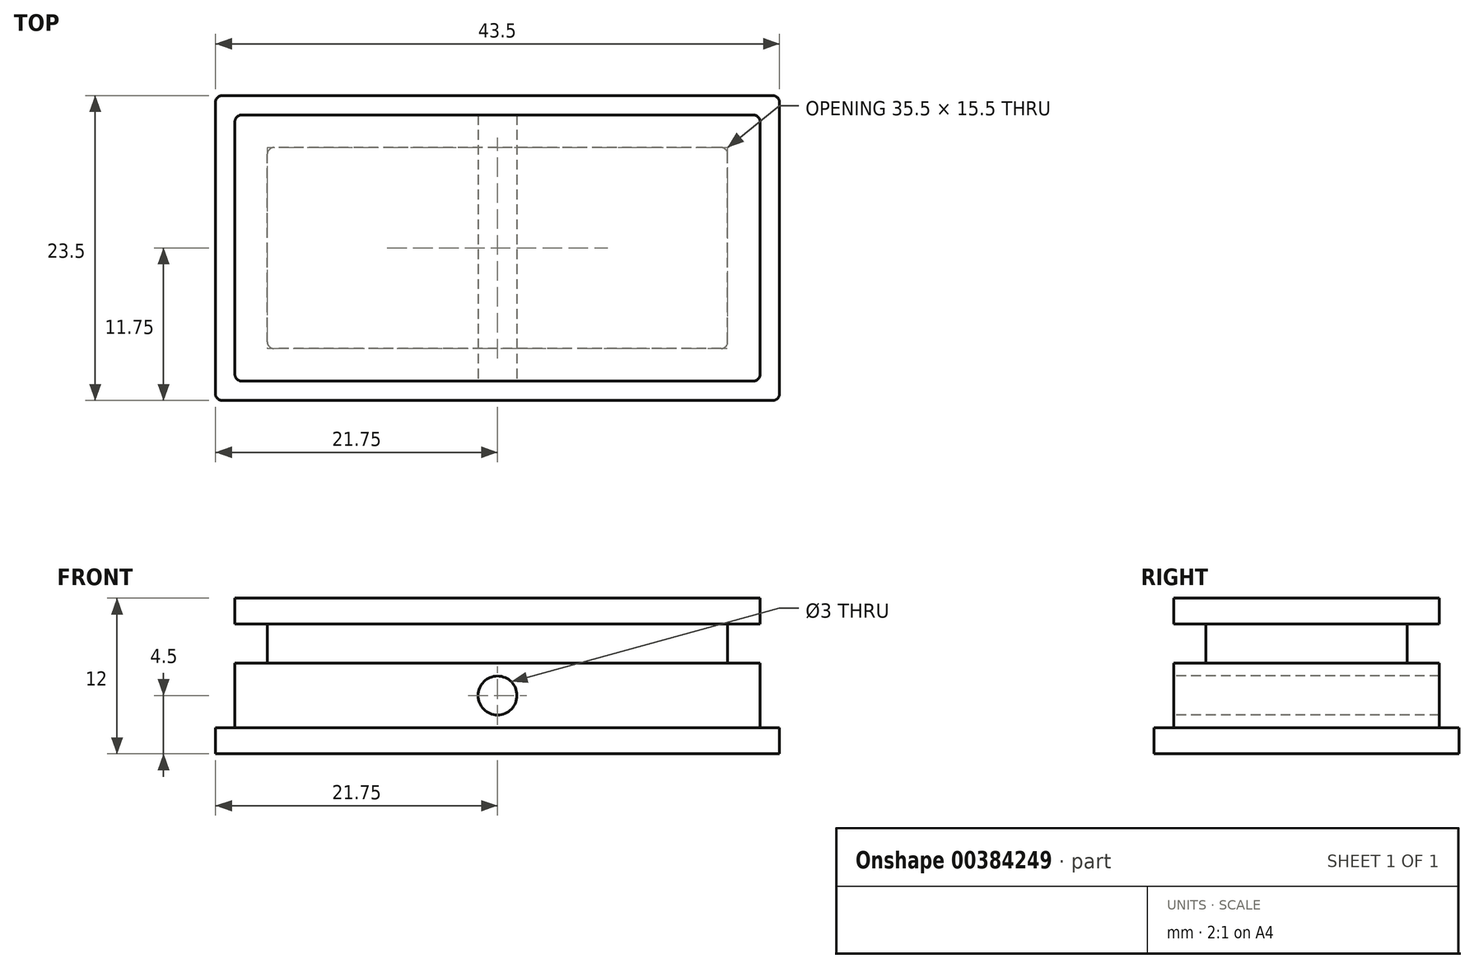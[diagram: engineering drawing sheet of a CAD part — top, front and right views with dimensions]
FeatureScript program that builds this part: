
annotation { "Feature Type Name" : "Feature", "Feature Type Description" : "" }
export const myFeature = defineFeature(function(context is Context, id is Id, definition is map)
    precondition{}
    {
        {
            var Q0;
            Q0=qCreatedBy(makeId("Top.planeOp"),FACE);
            var sketch = newSketch(context, id + "F0", { "sketchPlane" : qUnion([Q0])});
            skLineSegment(sketch, "E0.bottom", {"start": v(21.75, -11.75) * mm, "end": v(-21.75, -11.75) * mm});
            skLineSegment(sketch, "E0.top", {"start": v(21.75, 11.75) * mm, "end": v(-21.75, 11.75) * mm});
            skLineSegment(sketch, "E0.left", {"start": v(21.75, -11.75) * mm, "end": v(21.75, 11.75) * mm});
            skLineSegment(sketch, "E0.right", {"start": v(-21.75, -11.75) * mm, "end": v(-21.75, 11.75) * mm});
            skPoint(sketch, "E0.middle", {"position": v(0, 0) * mm});
            skSolve(sketch);
        }
        {
            var Q0;
            Q0=qSketchRegion(id+"F0",true);
            extrude(context, id + "F1", {"entities" : qUnion([Q0]), "depth" : 2 * mm});
        }
        {
            var Q0;
            Q0=makeQuery(id+"F1.opExtrude","CAP_FACE",FACE,{"disambiguationData":[OSD([sQuery(id+"F0.wireOp",EDGE,"E0.bottom"),sQuery(id+"F0.wireOp",EDGE,"E0.top"),sQuery(id+"F0.wireOp",EDGE,"E0.left"),sQuery(id+"F0.wireOp",EDGE,"E0.right")])],"isStart":false});
            var sketch = newSketch(context, id + "F2", { "sketchPlane" : qUnion([Q0])});
            skLineSegment(sketch, "E1.bottom", {"start": v(21.75, -11.75) * mm, "end": v(-21.75, -11.75) * mm, "construction": true});
            skLineSegment(sketch, "E1.top", {"start": v(21.75, 11.75) * mm, "end": v(-21.75, 11.75) * mm, "construction": true});
            skLineSegment(sketch, "E1.left", {"start": v(21.75, -11.75) * mm, "end": v(21.75, 11.75) * mm, "construction": true});
            skLineSegment(sketch, "E1.right", {"start": v(-21.75, -11.75) * mm, "end": v(-21.75, 11.75) * mm, "construction": true});
            skPoint(sketch, "E1.middle", {"position": v(0, 0) * mm});
            skLineSegment(sketch, "E2.0", {"start": v(20.25, 10.25) * mm, "end": v(-20.25, 10.25) * mm});
            skLineSegment(sketch, "E2.1", {"start": v(20.25, -10.25) * mm, "end": v(20.25, 10.25) * mm});
            skLineSegment(sketch, "E2.2", {"start": v(20.25, -10.25) * mm, "end": v(-20.25, -10.25) * mm});
            skLineSegment(sketch, "E2.3", {"start": v(-20.25, -10.25) * mm, "end": v(-20.25, 10.25) * mm});
            skSolve(sketch);
        }
        {
            var Q0;
            Q0=qSketchRegion(id+"F2",true);
            extrude(context, id + "F3", {"entities" : qUnion([Q0]), "operationType" : NewBodyOperationType.ADD, "depth" : 5 * mm});
        }
        {
            var Q0;
            Q0=makeQuery(id+"F3.opExtrude","CAP_FACE",FACE,{"disambiguationData":[OSD([sQuery(id+"F2.wireOp",EDGE,"E2.0"),sQuery(id+"F2.wireOp",EDGE,"E2.1"),sQuery(id+"F2.wireOp",EDGE,"E2.2"),sQuery(id+"F2.wireOp",EDGE,"E2.3")])],"isStart":false});
            var sketch = newSketch(context, id + "F4", { "sketchPlane" : qUnion([Q0])});
            skLineSegment(sketch, "E3.0", {"start": v(20.25, -10.25) * mm, "end": v(-20.25, -10.25) * mm, "construction": true});
            skLineSegment(sketch, "E4.0", {"start": v(-20.25, -10.25) * mm, "end": v(-20.25, 10.25) * mm, "construction": true});
            skLineSegment(sketch, "E5.0", {"start": v(20.25, 10.25) * mm, "end": v(-20.25, 10.25) * mm, "construction": true});
            skLineSegment(sketch, "E6.0", {"start": v(20.25, -10.25) * mm, "end": v(20.25, 10.25) * mm, "construction": true});
            skLineSegment(sketch, "E7.0", {"start": v(-17.75, -7.75) * mm, "end": v(-17.75, 7.75) * mm});
            skLineSegment(sketch, "E7.1", {"start": v(17.75, -7.75) * mm, "end": v(-17.75, -7.75) * mm});
            skLineSegment(sketch, "E7.2", {"start": v(17.75, -7.75) * mm, "end": v(17.75, 7.75) * mm});
            skLineSegment(sketch, "E7.3", {"start": v(17.75, 7.75) * mm, "end": v(-17.75, 7.75) * mm});
            skSolve(sketch);
        }
        {
            var Q0;
            Q0=qSketchRegion(id+"F4",true);
            var Q1;
            Q1=qConstructionFilter(qBodyType(qCreatedBy(id+"F4",EDGE),BodyType.WIRE),ConstructionObject.NO);
            extrude(context, id + "F5", {"entities" : qUnion([Q0]), "operationType" : NewBodyOperationType.ADD, "surfaceEntities" : qUnion([Q1]), "depth" : 3 * mm});
        }
        {
            var Q0;
            Q0=makeQuery(id+"F5.opExtrude","CAP_FACE",FACE,{"disambiguationData":[OSD([sQuery(id+"F4.wireOp",EDGE,"E7.0"),sQuery(id+"F4.wireOp",EDGE,"E7.1"),sQuery(id+"F4.wireOp",EDGE,"E7.2"),sQuery(id+"F4.wireOp",EDGE,"E7.3")])],"isStart":false});
            var sketch = newSketch(context, id + "F6", { "sketchPlane" : qUnion([Q0])});
            skLineSegment(sketch, "E8.0", {"start": v(20.25, -10.25) * mm, "end": v(-20.25, -10.25) * mm});
            skLineSegment(sketch, "E9.0", {"start": v(20.25, -10.25) * mm, "end": v(20.25, 10.25) * mm});
            skLineSegment(sketch, "E10.0", {"start": v(20.25, 10.25) * mm, "end": v(-20.25, 10.25) * mm});
            skLineSegment(sketch, "E10.1", {"start": v(-20.25, -10.25) * mm, "end": v(-20.25, 10.25) * mm});
            skSolve(sketch);
        }
        {
            var Q0;
            Q0=qSketchRegion(id+"F6",true);
            extrude(context, id + "F7", {"entities" : qUnion([Q0]), "operationType" : NewBodyOperationType.ADD, "depth" : 2 * mm});
        }
        {
            var Q0;
            Q0=makeQuery(id+"F3.opExtrude","SWEPT_EDGE",EDGE,{"disambiguationData":[OSD([sQuery(id+"F2.wireOp",EDGE,"E2.0"),sQuery(id+"F2.wireOp",EDGE,"E2.3")])]});
            var Q1;
            Q1=makeQuery(id+"F5.opExtrude","SWEPT_EDGE",EDGE,{"disambiguationData":[OSD([sQuery(id+"F4.wireOp",EDGE,"E7.0"),sQuery(id+"F4.wireOp",EDGE,"E7.3")])]});
            var Q2;
            Q2=makeQuery(id+"F7.opExtrude","SWEPT_EDGE",EDGE,{"disambiguationData":[OSD([sQuery(id+"F6.wireOp",EDGE,"E10.0"),sQuery(id+"F6.wireOp",EDGE,"E10.1")])]});
            var Q3;
            Q3=makeQuery(id+"F3.opExtrude","SWEPT_EDGE",EDGE,{"disambiguationData":[OSD([sQuery(id+"F2.wireOp",EDGE,"E2.2"),sQuery(id+"F2.wireOp",EDGE,"E2.3")])]});
            var Q4;
            Q4=makeQuery(id+"F5.opExtrude","SWEPT_EDGE",EDGE,{"disambiguationData":[OSD([sQuery(id+"F4.wireOp",EDGE,"E7.0"),sQuery(id+"F4.wireOp",EDGE,"E7.1")])]});
            var Q5;
            Q5=makeQuery(id+"F7.opExtrude","SWEPT_EDGE",EDGE,{"disambiguationData":[OSD([sQuery(id+"F6.wireOp",EDGE,"E8.0"),sQuery(id+"F6.wireOp",EDGE,"E10.1")])]});
            var Q6;
            Q6=makeQuery(id+"F3.opExtrude","SWEPT_EDGE",EDGE,{"disambiguationData":[OSD([sQuery(id+"F2.wireOp",EDGE,"E2.1"),sQuery(id+"F2.wireOp",EDGE,"E2.2")])]});
            var Q7;
            Q7=makeQuery(id+"F5.opExtrude","SWEPT_EDGE",EDGE,{"disambiguationData":[OSD([sQuery(id+"F4.wireOp",EDGE,"E7.1"),sQuery(id+"F4.wireOp",EDGE,"E7.2")])]});
            var Q8;
            Q8=makeQuery(id+"F7.opExtrude","SWEPT_EDGE",EDGE,{"disambiguationData":[OSD([sQuery(id+"F6.wireOp",EDGE,"E8.0"),sQuery(id+"F6.wireOp",EDGE,"E9.0")])]});
            var Q9;
            Q9=makeQuery(id+"F3.opExtrude","SWEPT_EDGE",EDGE,{"disambiguationData":[OSD([sQuery(id+"F2.wireOp",EDGE,"E2.0"),sQuery(id+"F2.wireOp",EDGE,"E2.1")])]});
            var Q10;
            Q10=makeQuery(id+"F5.opExtrude","SWEPT_EDGE",EDGE,{"disambiguationData":[OSD([sQuery(id+"F4.wireOp",EDGE,"E7.2"),sQuery(id+"F4.wireOp",EDGE,"E7.3")])]});
            var Q11;
            Q11=makeQuery(id+"F7.opExtrude","SWEPT_EDGE",EDGE,{"disambiguationData":[OSD([sQuery(id+"F6.wireOp",EDGE,"E9.0"),sQuery(id+"F6.wireOp",EDGE,"E10.0")])]});
            var Q12;
            Q12=makeQuery(id+"F1.opExtrude","SWEPT_EDGE",EDGE,{"disambiguationData":[OSD([sQuery(id+"F0.wireOp",EDGE,"E0.bottom"),sQuery(id+"F0.wireOp",EDGE,"E0.left")])]});
            var Q13;
            Q13=makeQuery(id+"F1.opExtrude","SWEPT_EDGE",EDGE,{"disambiguationData":[OSD([sQuery(id+"F0.wireOp",EDGE,"E0.top"),sQuery(id+"F0.wireOp",EDGE,"E0.left")])]});
            var Q14;
            Q14=makeQuery(id+"F1.opExtrude","SWEPT_EDGE",EDGE,{"disambiguationData":[OSD([sQuery(id+"F0.wireOp",EDGE,"E0.bottom"),sQuery(id+"F0.wireOp",EDGE,"E0.right")])]});
            var Q15;
            Q15=makeQuery(id+"F1.opExtrude","SWEPT_EDGE",EDGE,{"disambiguationData":[OSD([sQuery(id+"F0.wireOp",EDGE,"E0.top"),sQuery(id+"F0.wireOp",EDGE,"E0.right")])]});
            fillet(context, id + "F8", {"entities" : qUnion([Q0, Q1, Q2, Q3, Q4, Q5, Q6, Q7, Q8, Q9, Q10, Q11, Q12, Q13, Q14, Q15]), "radius" : 0.5 * mm, "tangentPropagation" : true, "allowEdgeOverflow" : false});
        }
        {
            var Q0;
            Q0=makeQuery(id+"F3.opExtrude","SWEPT_FACE",FACE,{"disambiguationData":[OSD([sQuery(id+"F2.wireOp",EDGE,"E2.2")])]});
            var sketch = newSketch(context, id + "F9", { "sketchPlane" : qUnion([Q0])});
            skLineSegment(sketch, "E11", {"start": v(0, 2) * mm, "end": v(0, 7) * mm, "construction": true});
            skCircle(sketch, "E12", {"center": v(0, 4.5) * mm, "radius": 1.5 * mm});
            skSolve(sketch);
        }
        {
            var Q0;
            Q0=qSketchRegion(id+"F9",true);
            extrude(context, id + "F10", {"entities" : qUnion([Q0]), "operationType" : NewBodyOperationType.REMOVE, "oppositeDirection" : true, "depth" : 25 * mm});
        }
    });
